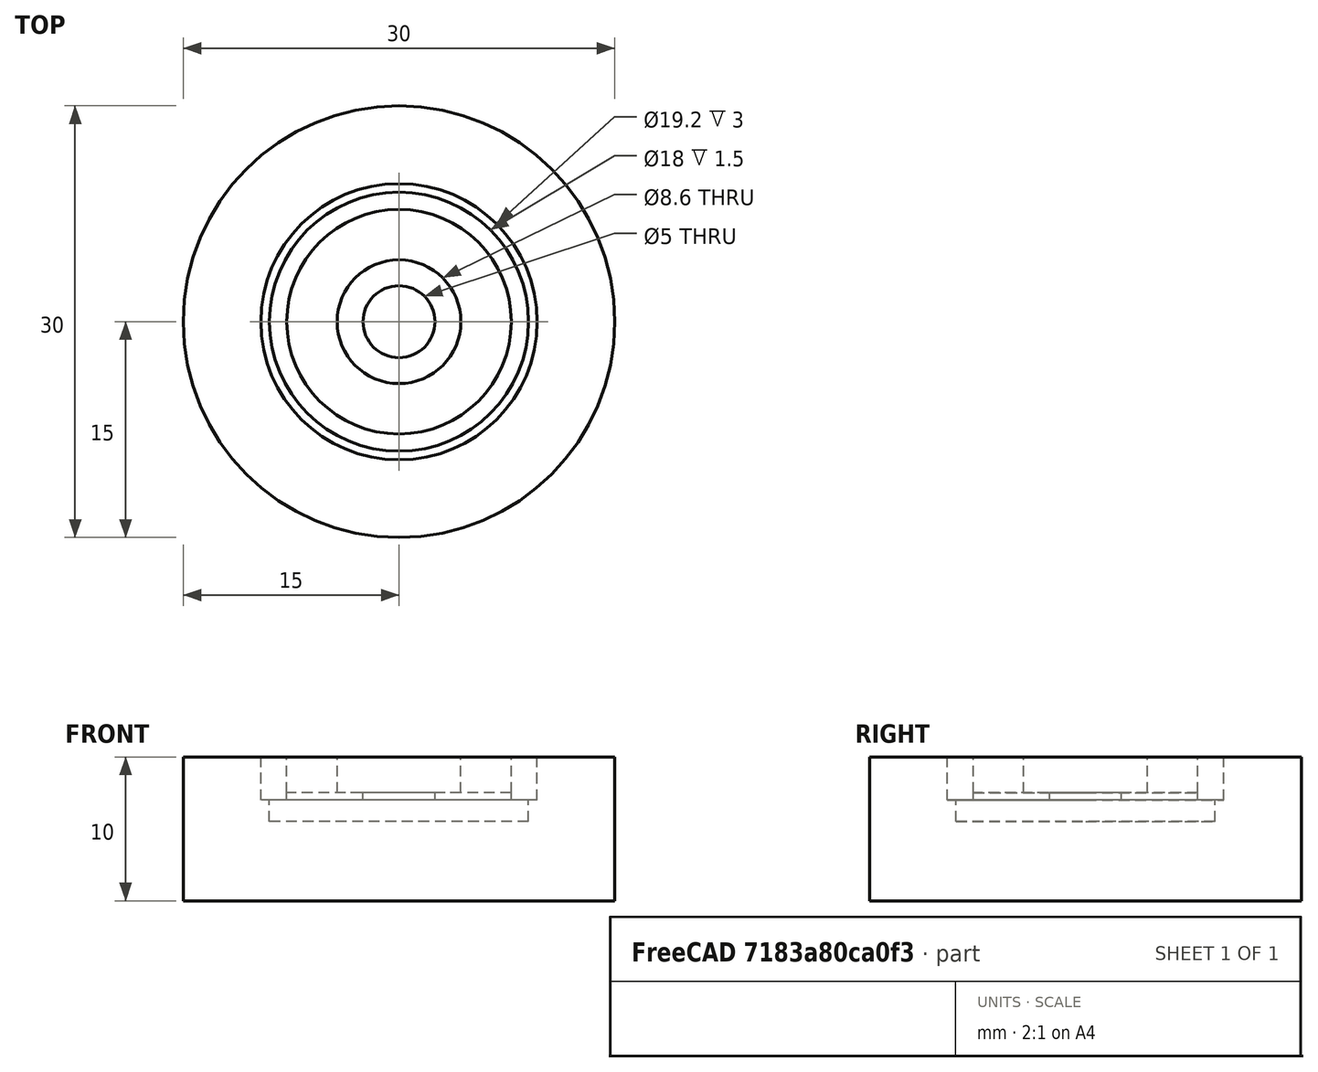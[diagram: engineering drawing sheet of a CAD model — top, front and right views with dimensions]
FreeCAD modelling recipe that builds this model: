
FCSTD DOCUMENT  (FreeCAD 0.17R13541 (Git))
Label: OPRAVKA
License: All rights reserved
LicenseURL: http://en.wikipedia.org/wiki/All_rights_reserved
objects: Drawing::FeatureViewPython×19, Part::Cylinder×7, Drawing::FeatureViewPart×6, Part::Cut×4, Drawing::FeaturePage×1
note: 11 computed .brp shape members not serialized (recipe doc carries the construction recipe); baked Part::Feature solids carry a one-line shape summary decoded from their .brp

FEATURE [Part::Cylinder] Cylinder
  Angle = 360
  AttacherType = Attacher::AttachEngine3D
  Height = 10
  Radius = 15
FEATURE [Part::Cylinder] Cylinder001
  Angle = 360
  AttacherType = Attacher::AttachEngine3D
  Height = 3
  Placement = pos=(0,0,7) rot=(0,0,1;0rad)
  Radius = 9.6
FEATURE [Part::Cut] Cut
  Base = -> Cylinder
  Tool = -> Cylinder001
FEATURE [Part::Cylinder] Cylinder002
  Angle = 360
  AttacherType = Attacher::AttachEngine3D
  Height = 1.5
  Placement = pos=(0,0,5.5) rot=(0,0,1;0rad)
  Radius = 9
FEATURE [Part::Cut] Cut001  label="PAD"
  Base = -> Cut
  Tool = -> Cylinder002
FEATURE [Part::Cylinder] Cylinder003
  Angle = 360
  AttacherType = Attacher::AttachEngine3D
  Height = 2.5
  Placement = pos=(0,0,7.5) rot=(0,0,1;0rad)
  Radius = 7.8
FEATURE [Part::Cylinder] Cylinder004
  Angle = 360
  AttacherType = Attacher::AttachEngine3D
  Height = 2.5
  Placement = pos=(0,0,7.5) rot=(0,0,1;0rad)
  Radius = 4.3
FEATURE [Part::Cut] Cut002  label="SHAIBA"
  Base = -> Cylinder003
  Tool = -> Cylinder004
FEATURE [Part::Cylinder] Cylinder005
  Angle = 360
  AttacherType = Attacher::AttachEngine3D
  Height = 0.5
  Placement = pos=(0,0,7) rot=(0,0,1;0rad)
  Radius = 7.8
FEATURE [Part::Cylinder] Cylinder006
  Angle = 360
  AttacherType = Attacher::AttachEngine3D
  Height = 0.5
  Placement = pos=(0,0,7) rot=(0,0,1;0rad)
  Radius = 2.5
FEATURE [Part::Cut] Cut003  label="PROKLADKA"
  Base = -> Cylinder005
  Tool = -> Cylinder006
FEATURE [Drawing::FeatureViewPart] Ortho  label="Ortho_0_0"
  Direction = (0,0,1)
  HiddenWidth = 0.15
  LineWidth = 0.35
  Rotation = 0
  Scale = 3
  ShowHiddenLines = true
  ShowSmoothLines = false
  Source = -> Cut001
  Tolerance = 0.05
  ViewResult = <g id="Ortho_0_0"\n   transform="rotate(0,78.5,78.3333) translate(78.5,78.3333) scale(3,3)"\n  >\n<g   fill="none"\n   stroke="rgb(0, 0, 0)"\n   stroke-dasharray="0.2,0.1)"\n   stroke-linecap="butt"\n   stroke-linejoin="miter"\n   stroke-width="0.050000"\n   transform="scale(1,-1)"\n  >\n<circle cx ="0" cy ="0" r ="15" /><circle cx ="0" cy ="0" r ="9.6" /><circle cx ="0" cy ="0" r ="9" /></g>\n<g   fill="none"\n   stroke="rgb(0, 0, 0)"\n   stroke-linecap="butt"\n   stroke-linejoin="miter"\n   stroke-width="0.116667"\n   transform="scale(1,-1)"\n  >\n<circle cx ="0" cy ="0" r ="15" /><circle cx ="0" cy ="0" r ="9.6" /><circle cx ="0" cy ="0" r ="9" /></g>\n</g>
  Visible = true
  X = 78.5
  Y = 78.3333
FEATURE [Drawing::FeatureViewPart] Ortho001  label="Ortho_0_-1"
  Direction = (0,-1,0)
  HiddenWidth = 0.15
  LineWidth = 0.35
  Rotation = 90
  Scale = 3
  ShowHiddenLines = true
  ShowSmoothLines = false
  Source = -> Cut001
  Tolerance = 0.05
  ViewResult = <blob: 3596 chars omitted>
  Visible = true
  X = 78.5
  Y = 176.667
FEATURE [Drawing::FeatureViewPython] dia001  # drawing view (typed FeaturePython)
  Rotation = 0
  ViewResult = <g>  <circle cx ="78.500000" cy ="78.333300" r="0.250000" stroke="none" fill="rgb(255,0,0)" /> \n<line x1="117.205485" y1="23.795498" x2="52.455831" y2="115.030728" style="stroke:rgb(255,0,0);stroke-width:0.10" />\n<polygon points="104.544169,41.635872 102.978901,42.977489 103.097271,43.674618 103.794400,43.556248" style="fill:rgb(255,0,0);stroke:rgb(255,0,0);stroke-width:0" />\n<polygon points="52.455831,115.030728 54.021099,113.689111 53.902729,112.991982 53.205600,113.110352" style="fill:rgb(255,0,0);stroke:rgb(255,0,0);stroke-width:0" />\n<line x1="117.205485" y1="23.795498" x2="143.785562" y2="23.795498" style="stroke:rgb(255,0,0);stroke-width:0.10" />\n<text x="130.495523" y="21.795498" font-family="inherit" font-size="3.6" fill="rgb(0,0,0)" text-anchor="middle" transform="rotate(0.000000 130.495523,21.795498)" >Ø30</text> </g>
  Visible = true
  X = 0
  Y = 0
  arrowL1 = 2
  arrowL2 = 0.5
  arrowW = 1
  arrow_scheme = 0
  autoPlaceOffset = 2
  autoPlaceText = true
  centerPointDia = 0.5
  click1_x = 117.205
  click1_y = 23.7955
  click2_x = 143.786
  click2_y = 23.7955
  click3_x = 143.786
  click3_y = 23.7955
  comma_decimal_place = false
  lineColor = rgb(255,0,0)
  strokeWidth = 0.1
  textFormat_circular = Ø%(value)3.3f
  textRenderer_color = rgb(0,0,0)
  textRenderer_family = inherit
  textRenderer_size = 3.6
  unit_custom_scale = 1
  unit_scheme = 0
FEATURE [Drawing::FeatureViewPython] dia002  # drawing view (typed FeaturePython)
  Rotation = 0
  ViewResult = <g>  <circle cx ="78.500000" cy ="78.333300" r="0.250000" stroke="none" fill="rgb(255,0,0)" /> \n<line x1="123.787218" y1="51.641293" x2="55.239561" y2="92.042859" style="stroke:rgb(255,0,0);stroke-width:0.10" />\n<polygon points="101.760439,64.623741 99.783562,65.208515 99.606694,65.893145 100.291324,66.070013" style="fill:rgb(255,0,0);stroke:rgb(255,0,0);stroke-width:0" />\n<polygon points="55.239561,92.042859 57.216438,91.458085 57.393306,90.773455 56.708676,90.596587" style="fill:rgb(255,0,0);stroke:rgb(255,0,0);stroke-width:0" />\n<line x1="123.787218" y1="51.641293" x2="140.241552" y2="51.641293" style="stroke:rgb(255,0,0);stroke-width:0.10" />\n<text x="132.014385" y="49.641293" font-family="inherit" font-size="3.6" fill="rgb(0,0,0)" text-anchor="middle" transform="rotate(0.000000 132.014385,49.641293)" >Ø18</text> </g>
  Visible = true
  X = 0
  Y = 0
  arrowL1 = 2
  arrowL2 = 0.5
  arrowW = 1
  arrow_scheme = 0
  autoPlaceOffset = 2
  autoPlaceText = true
  centerPointDia = 0.5
  click1_x = 123.787
  click1_y = 51.6413
  click2_x = 140.242
  click2_y = 51.8944
  click3_x = 140.242
  click3_y = 51.8944
  comma_decimal_place = false
  lineColor = rgb(255,0,0)
  strokeWidth = 0.1
  textFormat_circular = Ø%(value)3.3f
  textRenderer_color = rgb(0,0,0)
  textRenderer_family = inherit
  textRenderer_size = 3.6
  unit_custom_scale = 1
  unit_scheme = 0
FEATURE [Drawing::FeatureViewPython] dia003  # drawing view (typed FeaturePython)
  Rotation = 0
  ViewResult = <g>  <circle cx ="78.500000" cy ="78.333300" r="0.250000" stroke="none" fill="rgb(255,0,0)" /> \n<line x1="91.637982" y1="27.592652" x2="71.281044" y2="106.213879" style="stroke:rgb(255,0,0);stroke-width:0.10" />\n<polygon points="85.718956,50.452721 84.733602,52.263544 85.092311,52.872910 85.701678,52.514202" style="fill:rgb(255,0,0);stroke:rgb(255,0,0);stroke-width:0" />\n<polygon points="71.281044,106.213879 72.266398,104.403056 71.907689,103.793690 71.298322,104.152398" style="fill:rgb(255,0,0);stroke:rgb(255,0,0);stroke-width:0" />\n<line x1="91.637982" y1="27.592652" x2="107.332885" y2="27.592652" style="stroke:rgb(255,0,0);stroke-width:0.10" />\n<text x="99.485433" y="25.592652" font-family="inherit" font-size="3.6" fill="rgb(0,0,0)" text-anchor="middle" transform="rotate(0.000000 99.485433,25.592652)" >Ø19.2</text> </g>
  Visible = true
  X = 0
  Y = 0
  arrowL1 = 2
  arrowL2 = 0.5
  arrowW = 1
  arrow_scheme = 0
  autoPlaceOffset = 2
  autoPlaceText = true
  centerPointDia = 0.5
  click1_x = 91.638
  click1_y = 27.5927
  click2_x = 107.333
  click2_y = 26.8332
  click3_x = 107.333
  click3_y = 26.8332
  comma_decimal_place = false
  lineColor = rgb(255,0,0)
  strokeWidth = 0.1
  textFormat_circular = Ø%(value)3.3f
  textRenderer_color = rgb(0,0,0)
  textRenderer_family = inherit
  textRenderer_size = 3.6
  unit_custom_scale = 1
  unit_scheme = 0
FEATURE [Drawing::FeatureViewPython] dim001  # drawing view (typed FeaturePython)
  Rotation = 0
  ViewResult = <g> \n  <line x1="123.500000" y1="176.667000" x2="137.484635" y2="176.667000" style="stroke:rgb(255,0,0);stroke-width:0.10" />\n<line x1="123.500000" y1="146.667000" x2="137.484635" y2="146.667000" style="stroke:rgb(255,0,0);stroke-width:0.10" />\n<line x1="136.484635" y1="176.667000" x2="136.484635" y2="146.667000" style="stroke:rgb(255,0,0);stroke-width:0.10" /> \n  <polygon points="136.484635,146.667000 135.984635,148.667000 136.484635,149.167000 136.984635,148.667000" style="fill:rgb(255,0,0);stroke:rgb(255,0,0);stroke-width:0" /><polygon points="136.484635,176.667000 136.984635,174.667000 136.484635,174.167000 135.984635,174.667000" style="fill:rgb(255,0,0);stroke:rgb(255,0,0);stroke-width:0" /> \n  <text x="134.484635" y="161.667000" font-family="inherit" font-size="3.6" fill="rgb(0,0,0)" text-anchor="middle" transform="rotate(-90.000000 134.484635,161.667000)" >10</text> </g>
  Visible = true
  X = 0
  Y = 0
  arrowL1 = 2
  arrowL2 = 0.5
  arrowW = 1
  arrow_scheme = 0
  autoPlaceOffset = 2
  autoPlaceText = true
  click1_x = 136.485
  click1_y = 155.895
  click2_x = 136.485
  click2_y = 155.895
  comma_decimal_place = false
  dimension_line_overshoot = 1
  gap_datum_points = 0
  halfDimension_linear = false
  lineColor = rgb(255,0,0)
  strokeWidth = 0.1
  textFormat_linear = %(value)3.3f
  textRenderer_color = rgb(0,0,0)
  textRenderer_family = inherit
  textRenderer_size = 3.6
  unit_custom_scale = 1
  unit_scheme = 0
FEATURE [Drawing::FeatureViewPython] dim002  # drawing view (typed FeaturePython)
  Rotation = 0
  ViewResult = <g> \n  <line x1="51.500000" y1="160.167000" x2="42.999407" y2="160.167000" style="stroke:rgb(255,0,0);stroke-width:0.10" />\n<line x1="51.500000" y1="155.667000" x2="42.999407" y2="155.667000" style="stroke:rgb(255,0,0);stroke-width:0.10" />\n<line x1="43.999407" y1="160.167000" x2="43.999407" y2="155.667000" style="stroke:rgb(255,0,0);stroke-width:0.10" /> \n  <polygon points="43.999407,155.667000 44.499407,153.667000 43.999407,153.167000 43.499407,153.667000" style="fill:rgb(255,0,0);stroke:rgb(255,0,0);stroke-width:0" /><polygon points="43.999407,160.167000 43.499407,162.167000 43.999407,162.667000 44.499407,162.167000" style="fill:rgb(255,0,0);stroke:rgb(255,0,0);stroke-width:0" /> \n  <text x="41.999407" y="157.917000" font-family="inherit" font-size="3.6" fill="rgb(0,0,0)" text-anchor="middle" transform="rotate(-90.000000 41.999407,157.917000)" >1.5</text> </g>
  Visible = true
  X = 0
  Y = 0
  arrowL1 = 2
  arrowL2 = 0.5
  arrowW = 1
  arrow_scheme = 0
  autoPlaceOffset = 2
  autoPlaceText = true
  click1_x = 43.9994
  click1_y = 157.601
  click2_x = 43.9994
  click2_y = 157.601
  comma_decimal_place = false
  dimension_line_overshoot = 1
  gap_datum_points = 0
  halfDimension_linear = false
  lineColor = rgb(255,0,0)
  strokeWidth = 0.1
  textFormat_linear = %(value)3.3f
  textRenderer_color = rgb(0,0,0)
  textRenderer_family = inherit
  textRenderer_size = 3.6
  unit_custom_scale = 1
  unit_scheme = 0
FEATURE [Drawing::FeatureViewPython] dim003  # drawing view (typed FeaturePython)
  Rotation = 0
  ViewResult = <g> \n  <line x1="49.700000" y1="155.667000" x2="43.084185" y2="155.667000" style="stroke:rgb(255,0,0);stroke-width:0.10" />\n<line x1="49.700000" y1="146.667000" x2="43.084185" y2="146.667000" style="stroke:rgb(255,0,0);stroke-width:0.10" />\n<line x1="44.084185" y1="155.667000" x2="44.084185" y2="146.667000" style="stroke:rgb(255,0,0);stroke-width:0.10" /> \n  <polygon points="44.084185,146.667000 43.584185,148.667000 44.084185,149.167000 44.584185,148.667000" style="fill:rgb(255,0,0);stroke:rgb(255,0,0);stroke-width:0" /><polygon points="44.084185,155.667000 44.584185,153.667000 44.084185,153.167000 43.584185,153.667000" style="fill:rgb(255,0,0);stroke:rgb(255,0,0);stroke-width:0" /> \n  <text x="42.084185" y="151.167000" font-family="inherit" font-size="3.6" fill="rgb(0,0,0)" text-anchor="middle" transform="rotate(-90.000000 42.084185,151.167000)" >3</text> </g>
  Visible = true
  X = 0
  Y = 0
  arrowL1 = 2
  arrowL2 = 0.5
  arrowW = 1
  arrow_scheme = 0
  autoPlaceOffset = 2
  autoPlaceText = true
  click1_x = 44.0842
  click1_y = 151.582
  click2_x = 44.0842
  click2_y = 151.582
  comma_decimal_place = false
  dimension_line_overshoot = 1
  gap_datum_points = 0
  halfDimension_linear = false
  lineColor = rgb(255,0,0)
  strokeWidth = 0.1
  textFormat_linear = %(value)3.3f
  textRenderer_color = rgb(0,0,0)
  textRenderer_family = inherit
  textRenderer_size = 3.6
  unit_custom_scale = 1
  unit_scheme = 0
FEATURE [Drawing::FeatureViewPython] dim004  # drawing view (typed FeaturePython)
  Rotation = 0
  ViewResult = <g> \n  <line x1="51.500000" y1="160.167000" x2="51.500000" y2="168.492773" style="stroke:rgb(255,0,0);stroke-width:0.10" />\n<line x1="105.500000" y1="160.167000" x2="105.500000" y2="168.492773" style="stroke:rgb(255,0,0);stroke-width:0.10" />\n<line x1="51.500000" y1="167.492773" x2="105.500000" y2="167.492773" style="stroke:rgb(255,0,0);stroke-width:0.10" /> \n  <polygon points="105.500000,167.492773 103.500000,166.992773 103.000000,167.492773 103.500000,167.992773" style="fill:rgb(255,0,0);stroke:rgb(255,0,0);stroke-width:0" /><polygon points="51.500000,167.492773 53.500000,167.992773 54.000000,167.492773 53.500000,166.992773" style="fill:rgb(255,0,0);stroke:rgb(255,0,0);stroke-width:0" /> \n  <text x="78.500000" y="165.492773" font-family="inherit" font-size="3.6" fill="rgb(0,0,0)" text-anchor="middle" transform="rotate(0.000000 78.500000,165.492773)" >18</text> </g>
  Visible = true
  X = 0
  Y = 0
  arrowL1 = 2
  arrowL2 = 0.5
  arrowW = 1
  arrow_scheme = 0
  autoPlaceOffset = 2
  autoPlaceText = true
  click1_x = 105.599
  click1_y = 167.493
  click2_x = 105.599
  click2_y = 167.493
  comma_decimal_place = false
  dimension_line_overshoot = 1
  gap_datum_points = 0
  halfDimension_linear = false
  lineColor = rgb(255,0,0)
  strokeWidth = 0.1
  textFormat_linear = %(value)3.3f
  textRenderer_color = rgb(0,0,0)
  textRenderer_family = inherit
  textRenderer_size = 3.6
  unit_custom_scale = 1
  unit_scheme = 0
FEATURE [Drawing::FeatureViewPython] dim005  # drawing view (typed FeaturePython)
  Rotation = 0
  ViewResult = <g> \n  <line x1="107.300000" y1="146.667000" x2="107.300000" y2="137.437904" style="stroke:rgb(255,0,0);stroke-width:0.10" />\n<line x1="49.700000" y1="146.667000" x2="49.700000" y2="137.437904" style="stroke:rgb(255,0,0);stroke-width:0.10" />\n<line x1="107.300000" y1="138.437904" x2="49.700000" y2="138.437904" style="stroke:rgb(255,0,0);stroke-width:0.10" /> \n  <polygon points="49.700000,138.437904 51.700000,138.937904 52.200000,138.437904 51.700000,137.937904" style="fill:rgb(255,0,0);stroke:rgb(255,0,0);stroke-width:0" /><polygon points="107.300000,138.437904 105.300000,137.937904 104.800000,138.437904 105.300000,138.937904" style="fill:rgb(255,0,0);stroke:rgb(255,0,0);stroke-width:0" /> \n  <text x="78.500000" y="136.437904" font-family="inherit" font-size="3.6" fill="rgb(0,0,0)" text-anchor="middle" transform="rotate(-0.000000 78.500000,136.437904)" >19.2</text> </g>
  Visible = true
  X = 0
  Y = 0
  arrowL1 = 2
  arrowL2 = 0.5
  arrowW = 1
  arrow_scheme = 0
  autoPlaceOffset = 2
  autoPlaceText = true
  click1_x = 49.4421
  click1_y = 138.438
  click2_x = 49.4421
  click2_y = 138.438
  comma_decimal_place = false
  dimension_line_overshoot = 1
  gap_datum_points = 0
  halfDimension_linear = false
  lineColor = rgb(255,0,0)
  strokeWidth = 0.1
  textFormat_linear = %(value)3.3f
  textRenderer_color = rgb(0,0,0)
  textRenderer_family = inherit
  textRenderer_size = 3.6
  unit_custom_scale = 1
  unit_scheme = 0
FEATURE [Drawing::FeatureViewPython] dim006  # drawing view (typed FeaturePython)
  Rotation = 0
  ViewResult = <g> \n  <line x1="33.500000" y1="176.667000" x2="33.500000" y2="187.170902" style="stroke:rgb(255,0,0);stroke-width:0.10" />\n<line x1="123.500000" y1="176.667000" x2="123.500000" y2="187.170902" style="stroke:rgb(255,0,0);stroke-width:0.10" />\n<line x1="33.500000" y1="186.170902" x2="123.500000" y2="186.170902" style="stroke:rgb(255,0,0);stroke-width:0.10" /> \n  <polygon points="123.500000,186.170902 121.500000,185.670902 121.000000,186.170902 121.500000,186.670902" style="fill:rgb(255,0,0);stroke:rgb(255,0,0);stroke-width:0" /><polygon points="33.500000,186.170902 35.500000,186.670902 36.000000,186.170902 35.500000,185.670902" style="fill:rgb(255,0,0);stroke:rgb(255,0,0);stroke-width:0" /> \n  <text x="78.500000" y="184.170902" font-family="inherit" font-size="3.6" fill="rgb(0,0,0)" text-anchor="middle" transform="rotate(0.000000 78.500000,184.170902)" >30</text> </g>
  Visible = true
  X = 0
  Y = 0
  arrowL1 = 2
  arrowL2 = 0.5
  arrowW = 1
  arrow_scheme = 0
  autoPlaceOffset = 2
  autoPlaceText = true
  click1_x = 123.056
  click1_y = 186.171
  click2_x = 123.056
  click2_y = 186.171
  comma_decimal_place = false
  dimension_line_overshoot = 1
  gap_datum_points = 0
  halfDimension_linear = false
  lineColor = rgb(255,0,0)
  strokeWidth = 0.1
  textFormat_linear = %(value)3.3f
  textRenderer_color = rgb(0,0,0)
  textRenderer_family = inherit
  textRenderer_size = 3.6
  unit_custom_scale = 1
  unit_scheme = 0
FEATURE [Drawing::FeatureViewPart] Ortho002  label="Ortho_0_001"
  Direction = (0,0,1)
  HiddenWidth = 0.15
  LineWidth = 0.35
  Rotation = 0
  Scale = 3
  ShowHiddenLines = true
  ShowSmoothLines = false
  Source = -> Cut002
  Tolerance = 0.05
  ViewResult = <g id="Ortho_0_001"\n   transform="rotate(0,180,60) translate(180,60) scale(3,3)"\n  >\n<g   fill="none"\n   stroke="rgb(0, 0, 0)"\n   stroke-dasharray="0.2,0.1)"\n   stroke-linecap="butt"\n   stroke-linejoin="miter"\n   stroke-width="0.050000"\n   transform="scale(1,-1)"\n  >\n<circle cx ="0" cy ="0" r ="7.8" /><circle cx ="0" cy ="0" r ="4.3" /></g>\n<g   fill="none"\n   stroke="rgb(0, 0, 0)"\n   stroke-linecap="butt"\n   stroke-linejoin="miter"\n   stroke-width="0.116667"\n   transform="scale(1,-1)"\n  >\n<circle cx ="0" cy ="0" r ="7.8" /><circle cx ="0" cy ="0" r ="4.3" /></g>\n</g>
  Visible = true
  X = 180
  Y = 60
FEATURE [Drawing::FeatureViewPart] Ortho003  label="Ortho_0_-002"
  Direction = (0,-1,0)
  HiddenWidth = 0.15
  LineWidth = 0.35
  Rotation = 90
  Scale = 3
  ShowHiddenLines = true
  ShowSmoothLines = false
  Source = -> Cut002
  Tolerance = 0.05
  ViewResult = <blob: 2819 chars omitted>
  Visible = true
  X = 180
  Y = 136.25
FEATURE [Drawing::FeatureViewPart] Ortho004  label="Ortho_0_002"
  Direction = (0,0,1)
  HiddenWidth = 0.15
  LineWidth = 0.35
  Rotation = 0
  Scale = 3
  ShowHiddenLines = true
  ShowSmoothLines = false
  Source = -> Cut003
  Tolerance = 0.05
  ViewResult = <g id="Ortho_0_002"\n   transform="rotate(0,249.962,60) translate(249.962,60) scale(3,3)"\n  >\n<g   fill="none"\n   stroke="rgb(0, 0, 0)"\n   stroke-dasharray="0.2,0.1)"\n   stroke-linecap="butt"\n   stroke-linejoin="miter"\n   stroke-width="0.050000"\n   transform="scale(1,-1)"\n  >\n<circle cx ="0" cy ="0" r ="7.8" /><circle cx ="0" cy ="0" r ="2.5" /></g>\n<g   fill="none"\n   stroke="rgb(0, 0, 0)"\n   stroke-linecap="butt"\n   stroke-linejoin="miter"\n   stroke-width="0.116667"\n   transform="scale(1,-1)"\n  >\n<circle cx ="0" cy ="0" r ="7.8" /><circle cx ="0" cy ="0" r ="2.5" /></g>\n</g>
  Visible = true
  X = 249.962
  Y = 60
FEATURE [Drawing::FeatureViewPart] Ortho005  label="Ortho_0_-003"
  Direction = (0,-1,0)
  HiddenWidth = 0.15
  LineWidth = 0.35
  Rotation = 90
  Scale = 3
  ShowHiddenLines = true
  ShowSmoothLines = false
  Source = -> Cut003
  Tolerance = 0.05
  ViewResult = <blob: 2779 chars omitted>
  Visible = true
  X = 249.962
  Y = 131.75
FEATURE [Drawing::FeatureViewPython] dia004  # drawing view (typed FeaturePython)
  Rotation = 0
  ViewResult = <g>  <circle cx ="180.000000" cy ="60.000000" r="0.250000" stroke="none" fill="rgb(255,0,0)" /> \n<line x1="205.299456" y1="29.364657" x2="171.785774" y2="69.946682" style="stroke:rgb(255,0,0);stroke-width:0.10" />\n<polygon points="188.214226,50.053318 186.555173,51.277058 186.622322,51.980970 187.326233,51.913820" style="fill:rgb(255,0,0);stroke:rgb(255,0,0);stroke-width:0" />\n<polygon points="171.785774,69.946682 173.444827,68.722942 173.377678,68.019030 172.673767,68.086180" style="fill:rgb(255,0,0);stroke:rgb(255,0,0);stroke-width:0" />\n<line x1="205.299456" y1="29.364657" x2="219.981785" y2="29.364657" style="stroke:rgb(255,0,0);stroke-width:0.10" />\n<text x="212.640620" y="27.364657" font-family="inherit" font-size="3.6" fill="rgb(0,0,0)" text-anchor="middle" transform="rotate(0.000000 212.640620,27.364657)" >Ø8.6</text> </g>
  Visible = true
  X = 0
  Y = 0
  arrowL1 = 2
  arrowL2 = 0.5
  arrowW = 1
  arrow_scheme = 0
  autoPlaceOffset = 2
  autoPlaceText = true
  centerPointDia = 0.5
  click1_x = 205.299
  click1_y = 29.3647
  click2_x = 219.982
  click2_y = 28.0989
  click3_x = 219.982
  click3_y = 28.0989
  comma_decimal_place = false
  lineColor = rgb(255,0,0)
  strokeWidth = 0.1
  textFormat_circular = Ø%(value)3.3f
  textRenderer_color = rgb(0,0,0)
  textRenderer_family = inherit
  textRenderer_size = 3.6
  unit_custom_scale = 1
  unit_scheme = 0
FEATURE [Drawing::FeatureViewPython] dia005  # drawing view (typed FeaturePython)
  Rotation = 0
  ViewResult = <g>  <circle cx ="180.000000" cy ="60.000000" r="0.250000" stroke="none" fill="rgb(255,0,0)" /> \n<line x1="204.286882" y1="15.441759" x2="168.801120" y2="80.546170" style="stroke:rgb(255,0,0);stroke-width:0.10" />\n<polygon points="191.198880,39.453830 189.802690,40.970621 190.002418,41.648934 190.680731,41.449206" style="fill:rgb(255,0,0);stroke:rgb(255,0,0);stroke-width:0" />\n<polygon points="168.801120,80.546170 170.197310,79.029379 169.997582,78.351066 169.319269,78.550794" style="fill:rgb(255,0,0);stroke:rgb(255,0,0);stroke-width:0" />\n<line x1="204.286882" y1="15.441759" x2="214.918913" y2="15.441759" style="stroke:rgb(255,0,0);stroke-width:0.10" />\n<text x="209.602897" y="13.441759" font-family="inherit" font-size="3.6" fill="rgb(0,0,0)" text-anchor="middle" transform="rotate(0.000000 209.602897,13.441759)" >Ø15.6</text> </g>
  Visible = true
  X = 0
  Y = 0
  arrowL1 = 2
  arrowL2 = 0.5
  arrowW = 1
  arrow_scheme = 0
  autoPlaceOffset = 2
  autoPlaceText = true
  centerPointDia = 0.5
  click1_x = 204.287
  click1_y = 15.4418
  click2_x = 214.919
  click2_y = 16.4543
  click3_x = 214.919
  click3_y = 16.4543
  comma_decimal_place = false
  lineColor = rgb(255,0,0)
  strokeWidth = 0.1
  textFormat_circular = Ø%(value)3.3f
  textRenderer_color = rgb(0,0,0)
  textRenderer_family = inherit
  textRenderer_size = 3.6
  unit_custom_scale = 1
  unit_scheme = 0
FEATURE [Drawing::FeatureViewPython] dia006  # drawing view (typed FeaturePython)
  Rotation = 0
  ViewResult = <g>  <circle cx ="249.962000" cy ="60.000000" r="0.250000" stroke="none" fill="rgb(255,0,0)" /> \n<line x1="265.800775" y1="30.630375" x2="246.402007" y2="66.601246" style="stroke:rgb(255,0,0);stroke-width:0.10" />\n<polygon points="253.521993,53.398754 252.132578,54.921753 252.335329,55.599169 253.012745,55.396419" style="fill:rgb(255,0,0);stroke:rgb(255,0,0);stroke-width:0" />\n<polygon points="246.402007,66.601246 247.791422,65.078247 247.588671,64.400831 246.911255,64.603581" style="fill:rgb(255,0,0);stroke:rgb(255,0,0);stroke-width:0" />\n<line x1="265.800775" y1="30.630375" x2="279.217386" y2="30.630375" style="stroke:rgb(255,0,0);stroke-width:0.10" />\n<text x="272.509081" y="28.630375" font-family="inherit" font-size="3.6" fill="rgb(0,0,0)" text-anchor="middle" transform="rotate(0.000000 272.509081,28.630375)" >Ø5</text> </g>
  Visible = true
  X = 0
  Y = 0
  arrowL1 = 2
  arrowL2 = 0.5
  arrowW = 1
  arrow_scheme = 0
  autoPlaceOffset = 2
  autoPlaceText = true
  centerPointDia = 0.5
  click1_x = 265.801
  click1_y = 30.6304
  click2_x = 279.217
  click2_y = 27.8458
  click3_x = 279.217
  click3_y = 27.8458
  comma_decimal_place = false
  lineColor = rgb(255,0,0)
  strokeWidth = 0.1
  textFormat_circular = Ø%(value)3.3f
  textRenderer_color = rgb(0,0,0)
  textRenderer_family = inherit
  textRenderer_size = 3.6
  unit_custom_scale = 1
  unit_scheme = 0
FEATURE [Drawing::FeatureViewPython] dia007  # drawing view (typed FeaturePython)
  Rotation = 0
  ViewResult = <g>  <circle cx ="249.962000" cy ="60.000000" r="0.250000" stroke="none" fill="rgb(255,0,0)" /> \n<line x1="269.851073" y1="39.237257" x2="244.773873" y2="65.416026" style="stroke:rgb(255,0,0);stroke-width:0.10" />\n<polygon points="255.150127,54.583974 253.405558,55.682372 253.420751,56.389316 254.127695,56.374123" style="fill:rgb(255,0,0);stroke:rgb(255,0,0);stroke-width:0" />\n<polygon points="244.773873,65.416026 246.518442,64.317628 246.503249,63.610684 245.796305,63.625877" style="fill:rgb(255,0,0);stroke:rgb(255,0,0);stroke-width:0" />\n<line x1="269.851073" y1="39.237257" x2="282.001965" y2="39.237257" style="stroke:rgb(255,0,0);stroke-width:0.10" />\n<text x="275.926519" y="37.237257" font-family="inherit" font-size="3.6" fill="rgb(0,0,0)" text-anchor="middle" transform="rotate(0.000000 275.926519,37.237257)" >Ø5</text> </g>
  Visible = true
  X = 0
  Y = 0
  arrowL1 = 2
  arrowL2 = 0.5
  arrowW = 1
  arrow_scheme = 0
  autoPlaceOffset = 2
  autoPlaceText = true
  centerPointDia = 0.5
  click1_x = 269.851
  click1_y = 39.2373
  click2_x = 282.002
  click2_y = 38.9841
  click3_x = 282.002
  click3_y = 38.9841
  comma_decimal_place = false
  lineColor = rgb(255,0,0)
  strokeWidth = 0.1
  textFormat_circular = Ø%(value)3.3f
  textRenderer_color = rgb(0,0,0)
  textRenderer_family = inherit
  textRenderer_size = 3.6
  unit_custom_scale = 1
  unit_scheme = 0
FEATURE [Drawing::FeatureViewPython] dim007  # drawing view (typed FeaturePython)
  Rotation = 0
  ViewResult = <g> \n  <line x1="156.600000" y1="113.750000" x2="147.224593" y2="113.750000" style="stroke:rgb(255,0,0);stroke-width:0.10" />\n<line x1="156.600000" y1="106.250000" x2="147.224593" y2="106.250000" style="stroke:rgb(255,0,0);stroke-width:0.10" />\n<line x1="148.224593" y1="113.750000" x2="148.224593" y2="106.250000" style="stroke:rgb(255,0,0);stroke-width:0.10" /> \n  <polygon points="148.224593,106.250000 147.724593,108.250000 148.224593,108.750000 148.724593,108.250000" style="fill:rgb(255,0,0);stroke:rgb(255,0,0);stroke-width:0" /><polygon points="148.224593,113.750000 148.724593,111.750000 148.224593,111.250000 147.724593,111.750000" style="fill:rgb(255,0,0);stroke:rgb(255,0,0);stroke-width:0" /> \n  <text x="146.224593" y="110.000000" font-family="inherit" font-size="3.6" fill="rgb(0,0,0)" text-anchor="middle" transform="rotate(-90.000000 146.224593,110.000000)" >2.5</text> </g>
  Visible = true
  X = 0
  Y = 0
  arrowL1 = 2
  arrowL2 = 0.5
  arrowW = 1
  arrow_scheme = 0
  autoPlaceOffset = 2
  autoPlaceText = true
  click1_x = 148.225
  click1_y = 109.363
  click2_x = 148.225
  click2_y = 109.363
  comma_decimal_place = false
  dimension_line_overshoot = 1
  gap_datum_points = 0
  halfDimension_linear = false
  lineColor = rgb(255,0,0)
  strokeWidth = 0.1
  textFormat_linear = %(value)3.3f
  textRenderer_color = rgb(0,0,0)
  textRenderer_family = inherit
  textRenderer_size = 3.6
  unit_custom_scale = 1
  unit_scheme = 0
FEATURE [Drawing::FeatureViewPython] dim008  # drawing view (typed FeaturePython)
  Rotation = 0
  ViewResult = <g> \n  <line x1="192.900000" y1="113.750000" x2="192.900000" y2="122.549996" style="stroke:rgb(255,0,0);stroke-width:0.10" />\n<line x1="167.100000" y1="113.750000" x2="167.100000" y2="122.549996" style="stroke:rgb(255,0,0);stroke-width:0.10" />\n<line x1="192.900000" y1="121.549996" x2="167.100000" y2="121.549996" style="stroke:rgb(255,0,0);stroke-width:0.10" /> \n  <polygon points="167.100000,121.549996 169.100000,122.049996 169.600000,121.549996 169.100000,121.049996" style="fill:rgb(255,0,0);stroke:rgb(255,0,0);stroke-width:0" /><polygon points="192.900000,121.549996 190.900000,121.049996 190.400000,121.549996 190.900000,122.049996" style="fill:rgb(255,0,0);stroke:rgb(255,0,0);stroke-width:0" /> \n  <text x="180.000000" y="119.549996" font-family="inherit" font-size="3.6" fill="rgb(0,0,0)" text-anchor="middle" transform="rotate(0.000000 180.000000,119.549996)" >8.6</text> </g>
  Visible = true
  X = 0
  Y = 0
  arrowL1 = 2
  arrowL2 = 0.5
  arrowW = 1
  arrow_scheme = 0
  autoPlaceOffset = 2
  autoPlaceText = true
  click1_x = 167.546
  click1_y = 121.55
  click2_x = 167.546
  click2_y = 121.55
  comma_decimal_place = false
  dimension_line_overshoot = 1
  gap_datum_points = 0
  halfDimension_linear = false
  lineColor = rgb(255,0,0)
  strokeWidth = 0.1
  textFormat_linear = %(value)3.3f
  textRenderer_color = rgb(0,0,0)
  textRenderer_family = inherit
  textRenderer_size = 3.6
  unit_custom_scale = 1
  unit_scheme = 0
FEATURE [Drawing::FeatureViewPython] dim009  # drawing view (typed FeaturePython)
  Rotation = 0
  ViewResult = <g> \n  <line x1="156.600000" y1="113.750000" x2="156.600000" y2="130.756334" style="stroke:rgb(255,0,0);stroke-width:0.10" />\n<line x1="203.400000" y1="113.750000" x2="203.400000" y2="130.756334" style="stroke:rgb(255,0,0);stroke-width:0.10" />\n<line x1="156.600000" y1="129.756334" x2="203.400000" y2="129.756334" style="stroke:rgb(255,0,0);stroke-width:0.10" /> \n  <polygon points="203.400000,129.756334 201.400000,129.256334 200.900000,129.756334 201.400000,130.256334" style="fill:rgb(255,0,0);stroke:rgb(255,0,0);stroke-width:0" /><polygon points="156.600000,129.756334 158.600000,130.256334 159.100000,129.756334 158.600000,129.256334" style="fill:rgb(255,0,0);stroke:rgb(255,0,0);stroke-width:0" /> \n  <text x="180.000000" y="127.756334" font-family="inherit" font-size="3.6" fill="rgb(0,0,0)" text-anchor="middle" transform="rotate(0.000000 180.000000,127.756334)" >15.6</text> </g>
  Visible = true
  X = 0
  Y = 0
  arrowL1 = 2
  arrowL2 = 0.5
  arrowW = 1
  arrow_scheme = 0
  autoPlaceOffset = 2
  autoPlaceText = true
  click1_x = 196.047
  click1_y = 129.756
  click2_x = 196.047
  click2_y = 129.756
  comma_decimal_place = false
  dimension_line_overshoot = 1
  gap_datum_points = 0
  halfDimension_linear = false
  lineColor = rgb(255,0,0)
  strokeWidth = 0.1
  textFormat_linear = %(value)3.3f
  textRenderer_color = rgb(0,0,0)
  textRenderer_family = inherit
  textRenderer_size = 3.6
  unit_custom_scale = 1
  unit_scheme = 0
FEATURE [Drawing::FeatureViewPython] dim010  # drawing view (typed FeaturePython)
  Rotation = 0
  ViewResult = <g> \n  <line x1="226.562000" y1="110.750000" x2="219.855930" y2="110.750000" style="stroke:rgb(255,0,0);stroke-width:0.10" />\n<line x1="226.562000" y1="109.250000" x2="219.855930" y2="109.250000" style="stroke:rgb(255,0,0);stroke-width:0.10" />\n<line x1="220.855930" y1="110.750000" x2="220.855930" y2="109.250000" style="stroke:rgb(255,0,0);stroke-width:0.10" /> \n  <polygon points="220.855930,109.250000 221.355930,107.250000 220.855930,106.750000 220.355930,107.250000" style="fill:rgb(255,0,0);stroke:rgb(255,0,0);stroke-width:0" /><polygon points="220.855930,110.750000 220.355930,112.750000 220.855930,113.250000 221.355930,112.750000" style="fill:rgb(255,0,0);stroke:rgb(255,0,0);stroke-width:0" /> \n  <text x="218.855930" y="110.000000" font-family="inherit" font-size="3.6" fill="rgb(0,0,0)" text-anchor="middle" transform="rotate(-90.000000 218.855930,110.000000)" >0.5</text> </g>
  Visible = true
  X = 0
  Y = 0
  arrowL1 = 2
  arrowL2 = 0.5
  arrowW = 1
  arrow_scheme = 0
  autoPlaceOffset = 2
  autoPlaceText = true
  click1_x = 220.856
  click1_y = 110.264
  click2_x = 220.856
  click2_y = 110.264
  comma_decimal_place = false
  dimension_line_overshoot = 1
  gap_datum_points = 0
  halfDimension_linear = false
  lineColor = rgb(255,0,0)
  strokeWidth = 0.1
  textFormat_linear = %(value)3.3f
  textRenderer_color = rgb(0,0,0)
  textRenderer_family = inherit
  textRenderer_size = 3.6
  unit_custom_scale = 1
  unit_scheme = 0
FEATURE [Drawing::FeatureViewPython] dim012  # drawing view (typed FeaturePython)
  Rotation = 0
  ViewResult = <g> \n  <line x1="242.462000" y1="110.750000" x2="242.462000" y2="121.497339" style="stroke:rgb(255,0,0);stroke-width:0.10" />\n<line x1="257.462000" y1="110.750000" x2="257.462000" y2="121.497339" style="stroke:rgb(255,0,0);stroke-width:0.10" />\n<line x1="242.462000" y1="120.497339" x2="257.462000" y2="120.497339" style="stroke:rgb(255,0,0);stroke-width:0.10" /> \n  <polygon points="257.462000,120.497339 255.462000,119.997339 254.962000,120.497339 255.462000,120.997339" style="fill:rgb(255,0,0);stroke:rgb(255,0,0);stroke-width:0" /><polygon points="242.462000,120.497339 244.462000,120.997339 244.962000,120.497339 244.462000,119.997339" style="fill:rgb(255,0,0);stroke:rgb(255,0,0);stroke-width:0" /> \n  <text x="249.962000" y="118.497339" font-family="inherit" font-size="3.6" fill="rgb(0,0,0)" text-anchor="middle" transform="rotate(0.000000 249.962000,118.497339)" >5</text> </g>
  Visible = true
  X = 0
  Y = 0
  arrowL1 = 2
  arrowL2 = 0.5
  arrowW = 1
  arrow_scheme = 0
  autoPlaceOffset = 2
  autoPlaceText = true
  click1_x = 255.389
  click1_y = 120.497
  click2_x = 255.389
  click2_y = 120.497
  comma_decimal_place = false
  dimension_line_overshoot = 1
  gap_datum_points = 0
  halfDimension_linear = false
  lineColor = rgb(255,0,0)
  strokeWidth = 0.1
  textFormat_linear = %(value)3.3f
  textRenderer_color = rgb(0,0,0)
  textRenderer_family = inherit
  textRenderer_size = 3.6
  unit_custom_scale = 1
  unit_scheme = 0
FEATURE [Drawing::FeatureViewPython] dim013  # drawing view (typed FeaturePython)
  Rotation = 0
  ViewResult = <g> \n  <line x1="226.562000" y1="110.750000" x2="226.562000" y2="130.719217" style="stroke:rgb(255,0,0);stroke-width:0.10" />\n<line x1="273.362000" y1="110.750000" x2="273.362000" y2="130.719217" style="stroke:rgb(255,0,0);stroke-width:0.10" />\n<line x1="226.562000" y1="129.719217" x2="273.362000" y2="129.719217" style="stroke:rgb(255,0,0);stroke-width:0.10" /> \n  <polygon points="273.362000,129.719217 271.362000,129.219217 270.862000,129.719217 271.362000,130.219217" style="fill:rgb(255,0,0);stroke:rgb(255,0,0);stroke-width:0" /><polygon points="226.562000,129.719217 228.562000,130.219217 229.062000,129.719217 228.562000,129.219217" style="fill:rgb(255,0,0);stroke:rgb(255,0,0);stroke-width:0" /> \n  <text x="249.962000" y="127.719217" font-family="inherit" font-size="3.6" fill="rgb(0,0,0)" text-anchor="middle" transform="rotate(0.000000 249.962000,127.719217)" >15.6</text> </g>
  Visible = true
  X = 0
  Y = 0
  arrowL1 = 2
  arrowL2 = 0.5
  arrowW = 1
  arrow_scheme = 0
  autoPlaceOffset = 2
  autoPlaceText = true
  click1_x = 252.975
  click1_y = 129.719
  click2_x = 252.975
  click2_y = 129.719
  comma_decimal_place = false
  dimension_line_overshoot = 1
  gap_datum_points = 0
  halfDimension_linear = false
  lineColor = rgb(255,0,0)
  strokeWidth = 0.1
  textFormat_linear = %(value)3.3f
  textRenderer_color = rgb(0,0,0)
  textRenderer_family = inherit
  textRenderer_size = 3.6
  unit_custom_scale = 1
  unit_scheme = 0
FEATURE [Drawing::FeaturePage] Page
  EditableTexts = Dr. Zoidberg | 16.02.2019 | x3.0 | ??? | Soldering Stuff | First iteration | Whole Parts | Sheet 1
  Group = -> [Ortho,Ortho001,dia001,dia002,dia003,dim001,dim002,dim003,dim004,dim005,dim006,Ortho002,Ortho003,Ortho004,Ortho005,dia004,dia005,dia006,dia007,dim007,dim008,dim009,dim010,dim012,dim013]
  Template = <path>
note: 1 file-system path scrubbed to <path> (originals preserved in the JSON sidecar)
